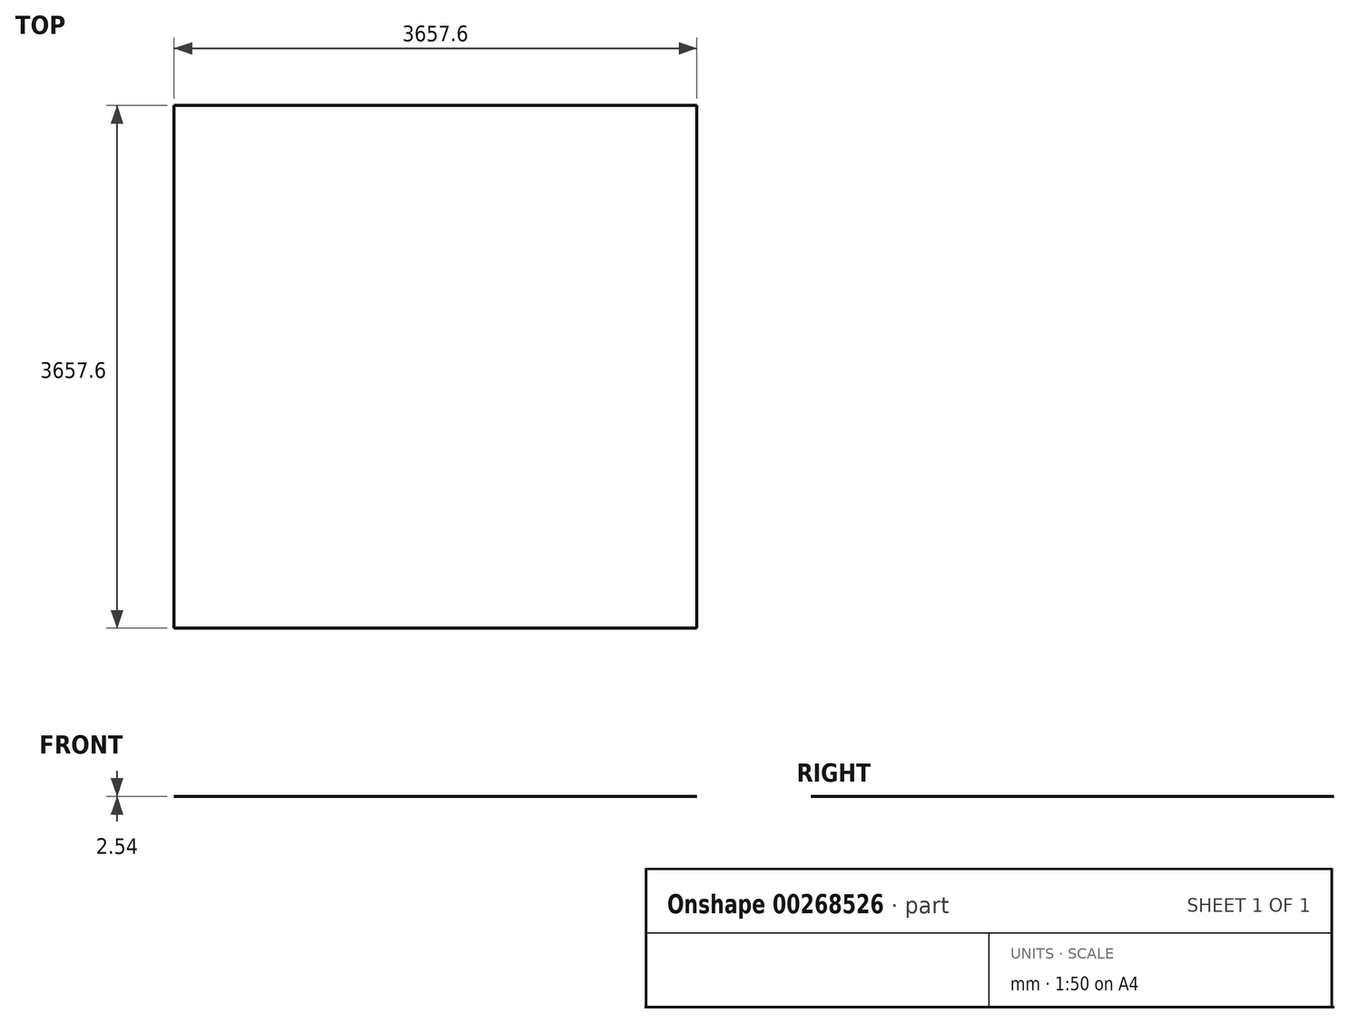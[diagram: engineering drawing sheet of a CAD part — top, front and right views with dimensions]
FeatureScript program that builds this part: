
annotation { "Feature Type Name" : "Feature", "Feature Type Description" : "" }
export const myFeature = defineFeature(function(context is Context, id is Id, definition is map)
    precondition{}
    {
        {
            var Q0;
            Q0=qCreatedBy(makeId("Top.planeOp"),FACE);
            var sketch = newSketch(context, id + "F0", { "sketchPlane" : qUnion([Q0])});
            skLineSegment(sketch, "E0.bottom", {"start": v(1828.8, 1828.8) * mm, "end": v(-1828.8, 1828.8) * mm});
            skLineSegment(sketch, "E0.top", {"start": v(1828.8, -1828.8) * mm, "end": v(-1828.8, -1828.8) * mm});
            skLineSegment(sketch, "E0.left", {"start": v(1828.8, 1828.8) * mm, "end": v(1828.8, -1828.8) * mm});
            skLineSegment(sketch, "E0.right", {"start": v(-1828.8, 1828.8) * mm, "end": v(-1828.8, -1828.8) * mm});
            skPoint(sketch, "E0.middle", {"position": v(0, 0) * mm});
            skSolve(sketch);
        }
        {
            var Q0;
            Q0 = qSketchRegion(id + "F0", true);
            extrude(context, id + "F1", {"entities" : qUnion([Q0]), "depth" : 2.54 * mm});
        }
    });
